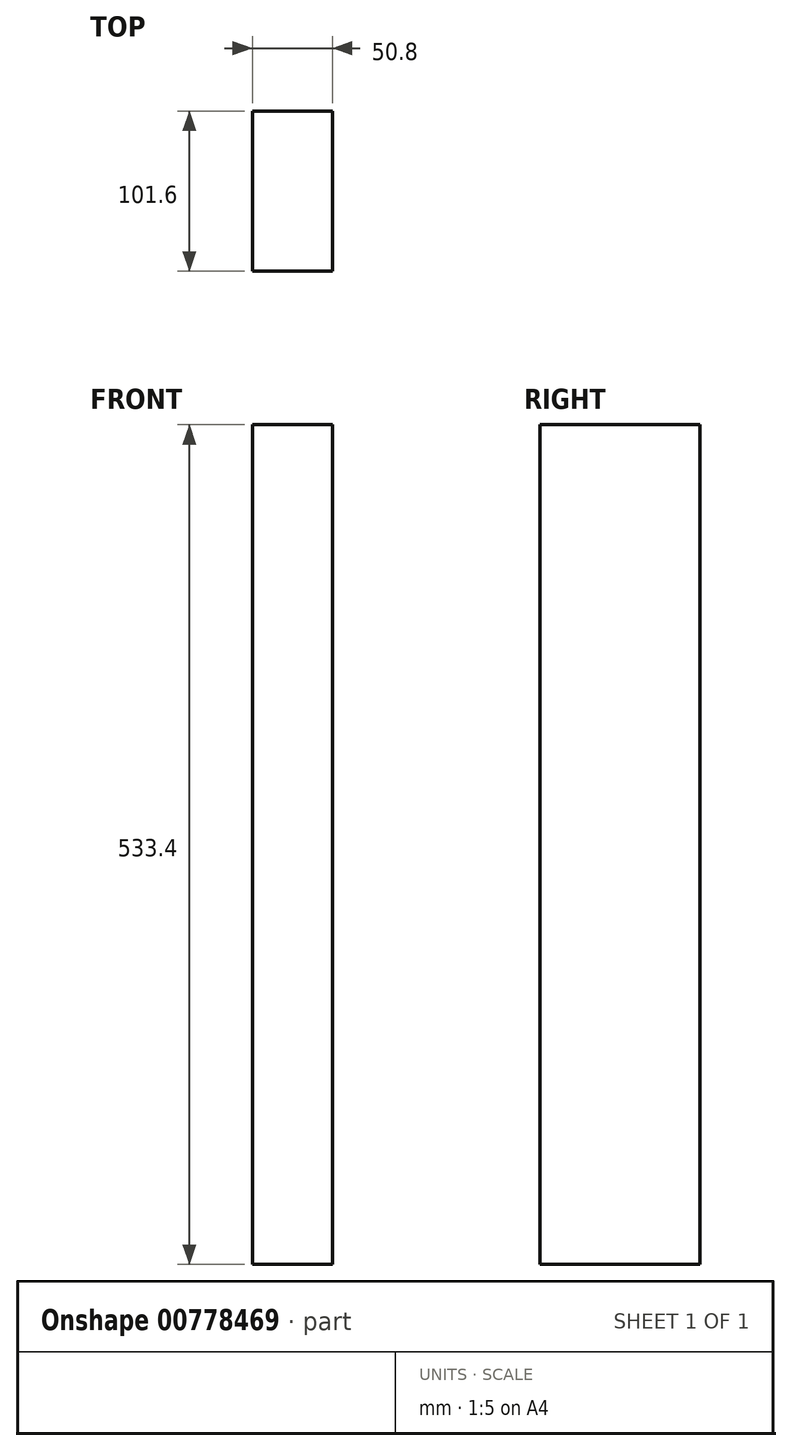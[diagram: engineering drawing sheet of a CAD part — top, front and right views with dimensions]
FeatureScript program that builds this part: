
annotation { "Feature Type Name" : "Feature", "Feature Type Description" : "" }
export const myFeature = defineFeature(function(context is Context, id is Id, definition is map)
    precondition{}
    {
        {
            var Q0;
            Q0=qCreatedBy(makeId("Front.planeOp"),FACE);
            var sketch = newSketch(context, id + "F0", { "sketchPlane" : qUnion([Q0])});
            skLineSegment(sketch, "E0.bottom", {"start": v(0, 0) * mm, "end": v(50.8, 0) * mm});
            skLineSegment(sketch, "E0.top", {"start": v(0, -533.4) * mm, "end": v(50.8, -533.4) * mm});
            skLineSegment(sketch, "E0.left", {"start": v(0, 0) * mm, "end": v(0, -533.4) * mm});
            skLineSegment(sketch, "E0.right", {"start": v(50.8, 0) * mm, "end": v(50.8, -533.4) * mm});
            skPoint(sketch, "E0.middle", {"position": v(25.4, -266.7) * mm});
            skSolve(sketch);
        }
        {
            var Q0;
            Q0 = qSketchRegion(id + "F0", true);
            extrude(context, id + "F1", {"entities" : qUnion([Q0]), "depth" : 101.6 * mm, "offsetDistance" : 25.4 * mm});
        }
    });
